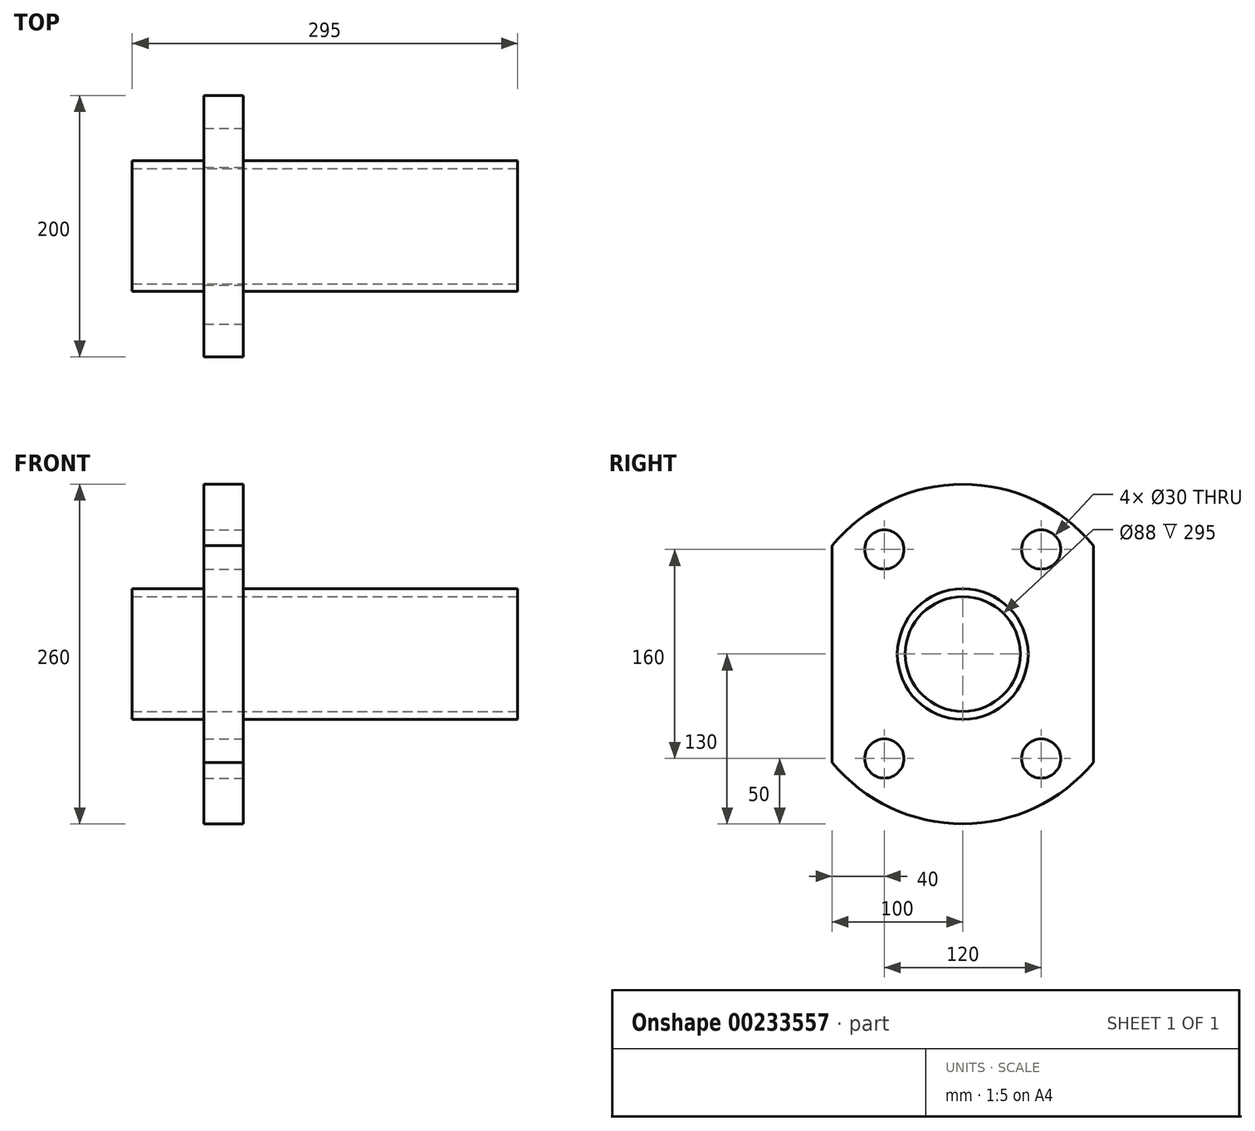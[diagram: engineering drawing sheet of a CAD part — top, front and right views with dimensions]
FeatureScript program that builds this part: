
annotation { "Feature Type Name" : "Feature", "Feature Type Description" : "" }
export const myFeature = defineFeature(function(context is Context, id is Id, definition is map)
    precondition{}
    {
        {
            var Q0;
            Q0=qCreatedBy(makeId("Right.planeOp"),FACE);
            var sketch = newSketch(context, id + "F0", { "sketchPlane" : qUnion([Q0])});
            skLineSegment(sketch, "E0.left", {"start": v(100, 83.07) * mm, "end": v(100, -83.07) * mm});
            skLineSegment(sketch, "E0.right", {"start": v(-100, 83.07) * mm, "end": v(-100, -83.07) * mm});
            skPoint(sketch, "E0.middle", {"position": v(0, 0) * mm});
            skCircle(sketch, "E1", {"center": v(0, 0) * mm, "radius": 50 * mm});
            skCircle(sketch, "E2", {"center": v(0, 0) * mm, "radius": 44 * mm});
            skArc(sketch, "E3", {"start": v(-100, 83.07) * mm, "mid": v(0, 130) * mm, "end": v(100, 83.07) * mm});
            skArc(sketch, "E4", {"start": v(-100, -83.07) * mm, "mid": v(0, -130) * mm, "end": v(100, -83.07) * mm});
            skLineSegment(sketch, "E5", {"start": v(0, 130) * mm, "end": v(0, -130) * mm, "construction": true});
            skLineSegment(sketch, "E6", {"start": v(-100, 0) * mm, "end": v(100, 0) * mm, "construction": true});
            skCircle(sketch, "E7", {"center": v(0, 0) * mm, "radius": 100 * mm, "construction": true});
            skCircle(sketch, "E8", {"center": v(-60, 80) * mm, "radius": 15 * mm, "construction": true});
            skCircle(sketch, "E9.MirrorC", {"center": v(60, 80) * mm, "radius": 15 * mm, "construction": true});
            skCircle(sketch, "E10.MirrorC", {"center": v(60, -80) * mm, "radius": 15 * mm, "construction": true});
            skCircle(sketch, "E11.MirrorC", {"center": v(-60, -80) * mm, "radius": 15 * mm, "construction": true});
            skSolve(sketch);
        }
        {
            var Q0;
            Q0=makeQuery(id+"F0.imprint","IMPRINT",FACE,{"disambiguationData":[TD([[makeQuery(id+"F0.imprint","IMPRINT",EDGE,{"derivedFrom":sQuery(id+"F0.wireOp",EDGE,"E0.left")}),-1.0]])]});
            var Q1;
            Q1=makeQuery(id+"F0.imprint","IMPRINT",FACE,{"disambiguationData":[TD([[makeQuery(id+"F0.imprint","IMPRINT",EDGE,{"derivedFrom":sQuery(id+"F0.wireOp",EDGE,"E1")}),1.0]])]});
            extrude(context, id + "F1", {"entities" : qUnion([Q0, Q1]), "oppositeDirection" : true, "depth" : 30 * mm});
        }
        {
            var Q0;
            Q0=sQuery(id+"F0.wireOp",VERTEX,"E8.center");
            var Q1;
            Q1=sQuery(id+"F0.wireOp",VERTEX,"E9.MirrorC.center");
            var Q2;
            Q2=sQuery(id+"F0.wireOp",VERTEX,"E10.MirrorC.center");
            var Q3;
            Q3=sQuery(id+"F0.wireOp",VERTEX,"E11.MirrorC.center");
            var Q4;
            Q4=makeQuery(id+"F1.opExtrude","SWEPT_BODY",BODY,{"disambiguationData":[OSD([sQuery(id+"F0.wireOp",EDGE,"E0.left"),sQuery(id+"F0.wireOp",EDGE,"E0.right"),sQuery(id+"F0.wireOp",EDGE,"E2"),sQuery(id+"F0.wireOp",EDGE,"E3"),sQuery(id+"F0.wireOp",EDGE,"E4")])]});
            hole(context, id + "F2", {"style" : HoleStyle.SIMPLE, "endStyle" : HoleEndStyle.THROUGH, "holeDiameter" : 30 * mm, "startFromSketch" : true, "locations" : qUnion([Q0, Q1, Q2, Q3]), "scope" : qUnion([Q4]), "isTappedThrough" : true});
        }
        {
            var Q0;
            Q0=makeQuery(id+"F0.imprint","IMPRINT",FACE,{"disambiguationData":[TD([[makeQuery(id+"F0.imprint","IMPRINT",EDGE,{"derivedFrom":sQuery(id+"F0.wireOp",EDGE,"E1")}),1.0]])]});
            extrude(context, id + "F3", {"entities" : qUnion([Q0]), "operationType" : NewBodyOperationType.ADD, "depth" : 210 * mm});
        }
        {
            var Q0;
            Q0=makeQuery(id+"F0.imprint","IMPRINT",FACE,{"disambiguationData":[TD([[makeQuery(id+"F0.imprint","IMPRINT",EDGE,{"derivedFrom":sQuery(id+"F0.wireOp",EDGE,"E1")}),1.0]])]});
            extrude(context, id + "F4", {"entities" : qUnion([Q0]), "operationType" : NewBodyOperationType.ADD, "oppositeDirection" : true, "depth" : 85 * mm});
        }
    });
